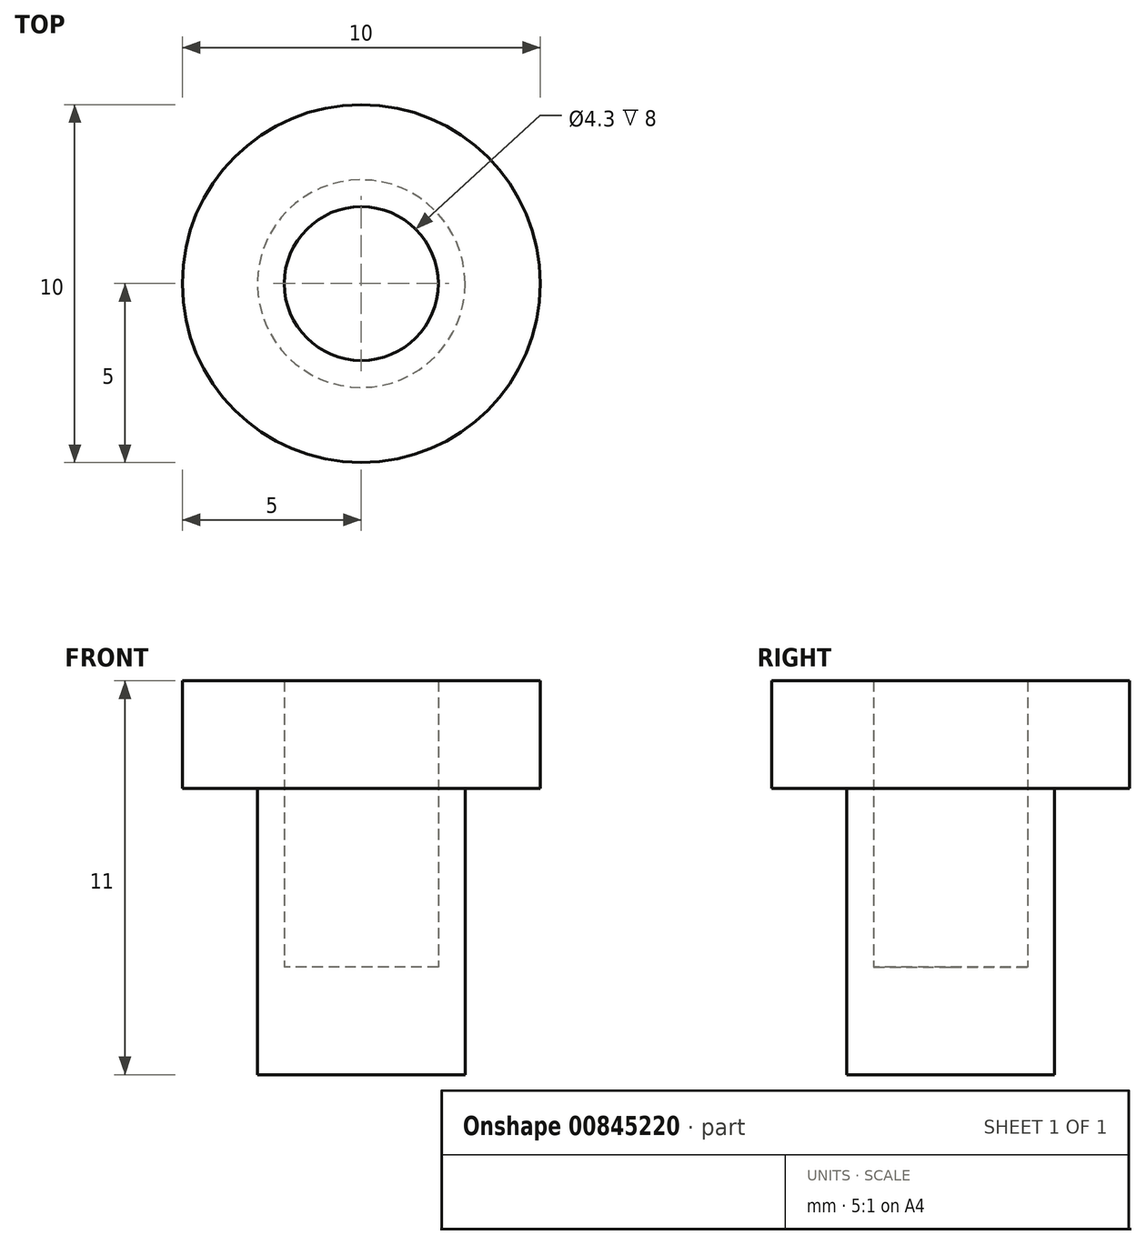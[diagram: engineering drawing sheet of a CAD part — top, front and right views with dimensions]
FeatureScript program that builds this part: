
annotation { "Feature Type Name" : "Feature", "Feature Type Description" : "" }
export const myFeature = defineFeature(function(context is Context, id is Id, definition is map)
    precondition{}
    {
        {
            var Q0;
            Q0=qCreatedBy(makeId("Top.planeOp"),FACE);
            var sketch = newSketch(context, id + "F0", { "sketchPlane" : qUnion([Q0])});
            skCircle(sketch, "E0", {"center": v(0, 0) * mm, "radius": 5 * mm});
            skCircle(sketch, "E1", {"center": v(0, 0) * mm, "radius": 2.9 * mm});
            skCircle(sketch, "E2", {"center": v(0, 0) * mm, "radius": 2.15 * mm});
            skSolve(sketch);
        }
        {
            var Q0;
            Q0=makeQuery(id+"F0.imprint","IMPRINT",FACE,{"disambiguationData":[TD([[makeQuery(id+"F0.imprint","IMPRINT",EDGE,{"derivedFrom":sQuery(id+"F0.wireOp",EDGE,"E0")}),1.0]])]});
            var Q1;
            Q1=makeQuery(id+"F0.imprint","IMPRINT",FACE,{"disambiguationData":[TD([[makeQuery(id+"F0.imprint","IMPRINT",EDGE,{"derivedFrom":sQuery(id+"F0.wireOp",EDGE,"E1")}),1.0]])]});
            extrude(context, id + "F1", {"entities" : qUnion([Q0, Q1]), "depth" : 3 * mm, "offsetDistance" : 25 * mm});
        }
        {
            var Q0;
            Q0=makeQuery(id+"F0.imprint","IMPRINT",FACE,{"disambiguationData":[TD([[makeQuery(id+"F0.imprint","IMPRINT",EDGE,{"derivedFrom":sQuery(id+"F0.wireOp",EDGE,"E1")}),1.0]])]});
            extrude(context, id + "F2", {"entities" : qUnion([Q0]), "operationType" : NewBodyOperationType.ADD, "oppositeDirection" : true, "depth" : 5 * mm, "offsetDistance" : 25 * mm});
        }
        {
            var Q0;
            Q0=makeQuery(id+"F2.opExtrude","CAP_FACE",FACE,{"disambiguationData":[OSD([sQuery(id+"F0.wireOp",EDGE,"E1"),sQuery(id+"F0.wireOp",EDGE,"E2")])],"isStart":false});
            var sketch = newSketch(context, id + "F3", { "sketchPlane" : qUnion([Q0])});
            skCircle(sketch, "E3", {"center": v(0, 0) * mm, "radius": 2.9 * mm});
            skSolve(sketch);
        }
        {
            var Q0;
            Q0 = qSketchRegion(id + "F3", true);
            extrude(context, id + "F4", {"entities" : qUnion([Q0]), "operationType" : NewBodyOperationType.ADD, "depth" : 3 * mm, "offsetDistance" : 25 * mm});
        }
    });
